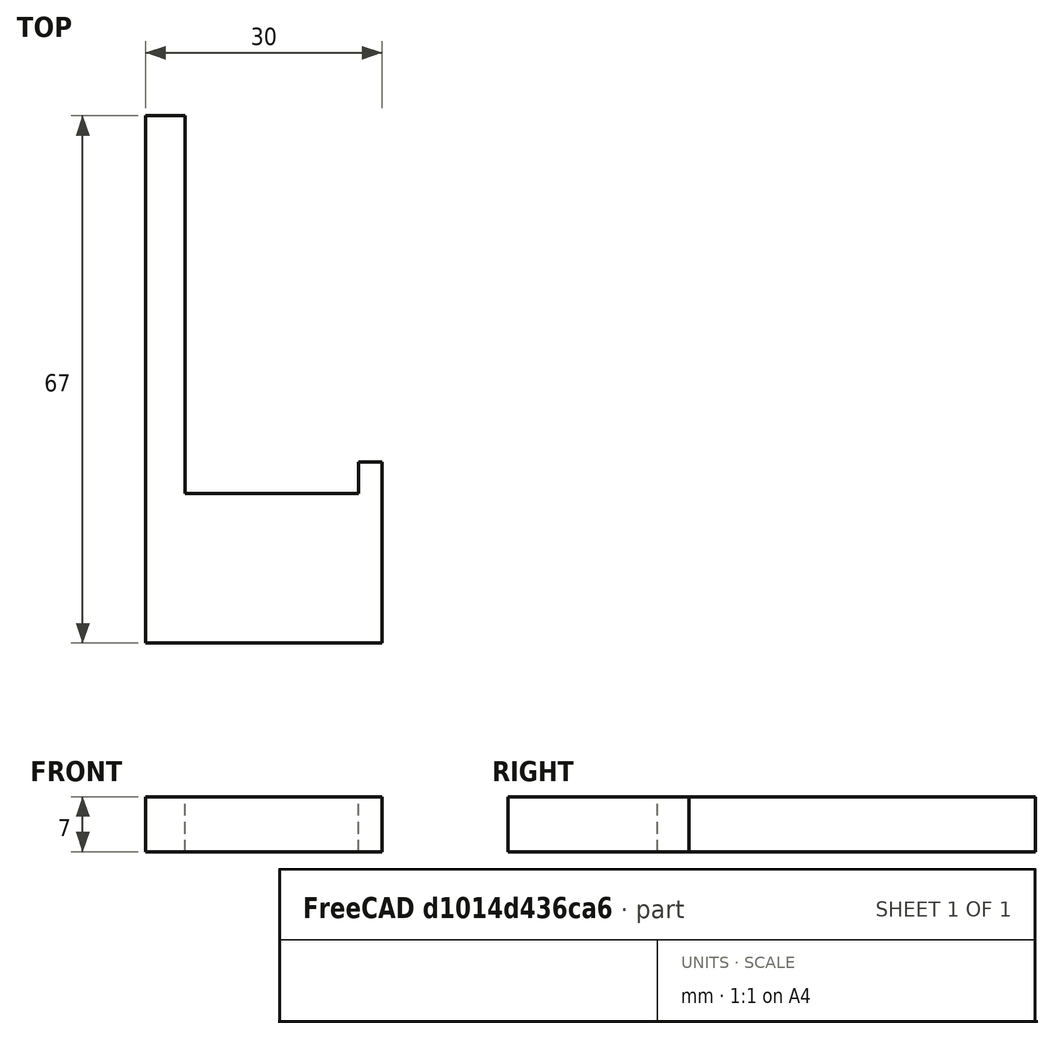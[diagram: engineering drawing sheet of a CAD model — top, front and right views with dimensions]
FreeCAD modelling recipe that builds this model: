
FCSTD DOCUMENT  (FreeCAD 0.21R33771 (Git))
Label: kitchenAirCookTopStablizer
License: All rights reserved
LicenseURL: http://en.wikipedia.org/wiki/All_rights_reserved
objects: Sketcher::SketchObject×1, Spreadsheet::Sheet×1, PartDesign::Pad×1, PartDesign::Body×1
note: 4 computed .brp shape members not serialized (recipe doc carries the construction recipe); baked Part::Feature solids carry a one-line shape summary decoded from their .brp

FEATURE [Sketcher::SketchObject] Sketch
  FullyConstrained = true
  MapMode = 5
  Support = -> [XY_Plane]
  expr: Constraints[10] = Spreadsheet.topGuardSideWidth
  expr: Constraints[17] = Spreadsheet.topGuardHeight + Spreadsheet.topGapHeight
  expr: Constraints[18] = Spreadsheet.longSideArmLen
  expr: Constraints[1] = Spreadsheet.topGap
  expr: Constraints[21] = Spreadsheet.longSideArmWidth
  expr: Constraints[7] = Spreadsheet.topGuardHeight
  sketch-geometry (8):
    g0: LineSegment StartX=-11 StartY=0 StartZ=0 EndX=11 EndY=0 EndZ=0
    g1: LineSegment StartX=-11 StartY=0 StartZ=0 EndX=-11 EndY=48 EndZ=0
    g2: LineSegment StartX=11 StartY=0 StartZ=0 EndX=11 EndY=4 EndZ=0
    g3: LineSegment StartX=11 StartY=4 StartZ=0 EndX=14 EndY=4 EndZ=0
    g4: LineSegment StartX=14 StartY=4 StartZ=0 EndX=14 EndY=-19 EndZ=0
    g5: LineSegment StartX=-16 StartY=48 StartZ=0 EndX=-16 EndY=-19 EndZ=0
    g6: LineSegment StartX=-16 StartY=-19 StartZ=0 EndX=14 EndY=-19 EndZ=0
    g7: LineSegment StartX=-11 StartY=48 StartZ=0 EndX=-16 EndY=48 EndZ=0
  constraints (23):
    c: PointOnObject(g0,g-1)
    c: DistanceX(g0,g0) = 22
    c: Symmetric(g0,g0,g-2)
    c: Coincident(g1,g0)
    c: Coincident(g2,g0)
    c: Vertical(g1)
    c: Vertical(g2)
    c: DistanceY(g2,g2) = 4
    c: Coincident(g3,g2)
    c: Horizontal(g3)
    c: DistanceX(g3,g3) = 3
    c: Coincident(g4,g3)
    c: Vertical(g5)
    c: Vertical(g4)
    c: Coincident(g6,g5)
    c: Coincident(g6,g4)
    c: Horizontal(g6)
    c: DistanceY(g4,g4) = 23
    c: DistanceY(g1,g1) = 48
    c: Coincident(g7,g1)
    c: Horizontal(g7)
    c: DistanceX(g7,g7) = 5
    c: Coincident(g5,g7)
FEATURE [Spreadsheet::Sheet] Spreadsheet
  cells = A2='topGapHeight; B2(topGapHeight)=19; C2='was 15,too lose, 17; D2='height; A3='topGap; B3(topGap)=22; C3='was 17, 19,21; A4='pad; B4(pad)=7; A5='topGuardHeight; B5(topGuardHeight)=4; A6='topGuardSideWidth; B6(topGuardSideWidth)=3; A8='longSideArmLen; B8(longSideArmLen)=48; A9='longSideArmWidth; B9(longSideArmWidth)=5
FEATURE [PartDesign::Pad] Pad
  Direction = (0,0,1)
  Length = 7
  Length2 = 10
  Profile = -> Sketch
  ReferenceAxis = -> Sketch [N_Axis]
  Type = 0
  expr: Length = Spreadsheet.pad
FEATURE [PartDesign::Body] Body
  Group = -> [Sketch,Pad]
  Origin = -> Origin
  Tip = -> Pad
